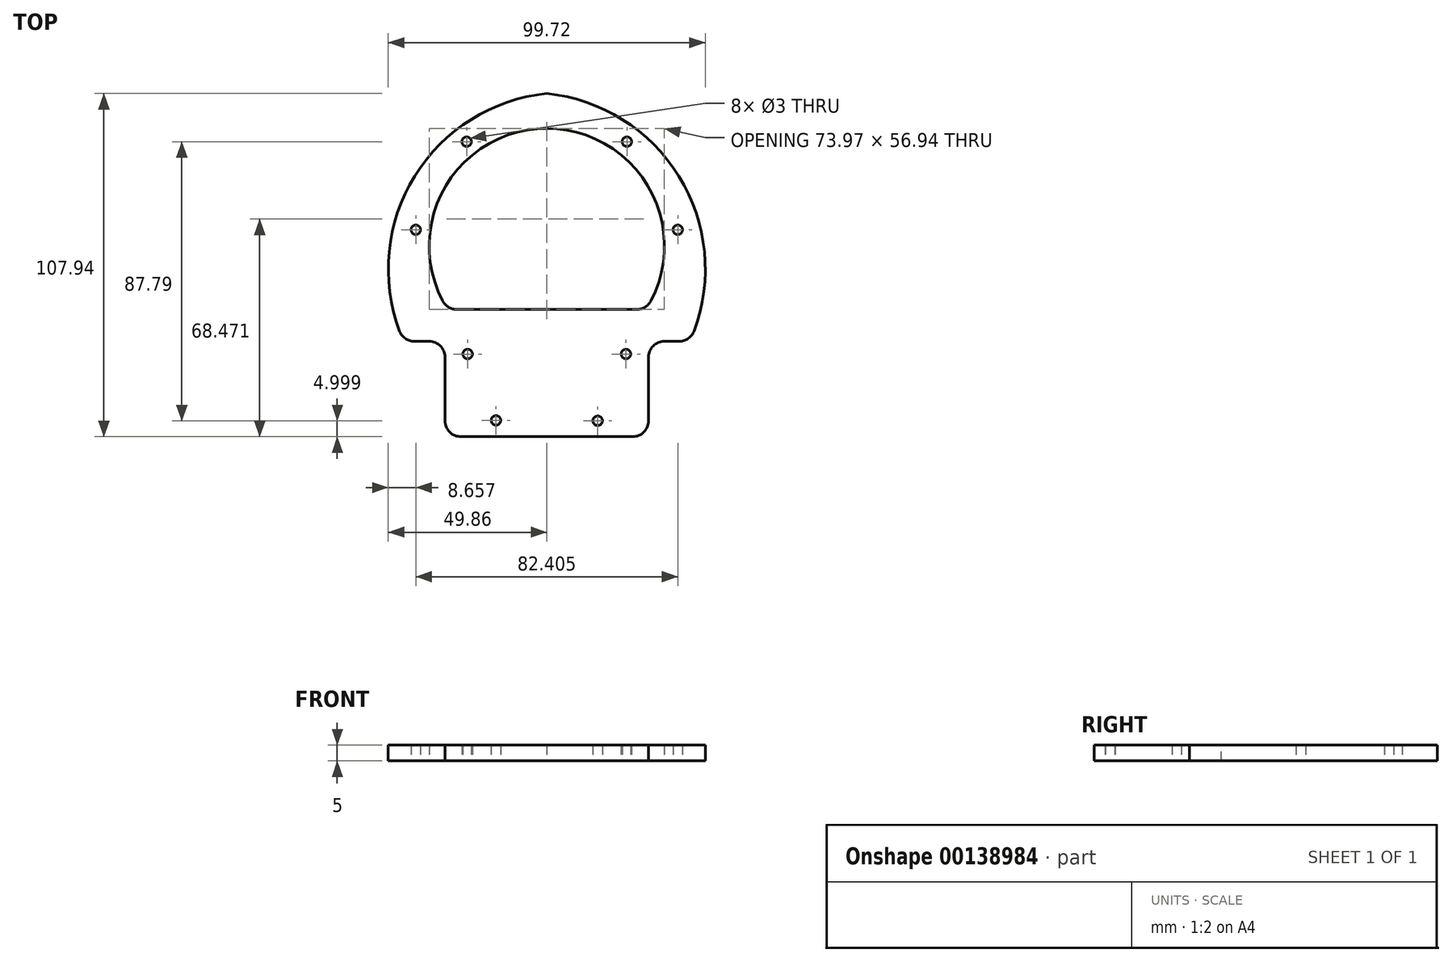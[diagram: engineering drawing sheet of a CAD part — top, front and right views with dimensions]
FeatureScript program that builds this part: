
annotation { "Feature Type Name" : "Feature", "Feature Type Description" : "" }
export const myFeature = defineFeature(function(context is Context, id is Id, definition is map)
    precondition{}
    {
        {
            var Q0;
            Q0=qCreatedBy(makeId("Top.planeOp"),FACE);
            var sketch = newSketch(context, id + "F0", { "sketchPlane" : qUnion([Q0])});
            skLineSegment(sketch, "E0.0", {"start": v(45, -25.98) * mm, "end": v(-45, -25.98) * mm});
            skLineSegment(sketch, "E0.1", {"start": v(-45, -25.98) * mm, "end": v(0, 51.96) * mm});
            skLineSegment(sketch, "E0.2", {"start": v(0, 51.96) * mm, "end": v(45, -25.98) * mm});
            skPoint(sketch, "E0.0.midPoint", {"position": v(0, -25.98) * mm});
            skLineSegment(sketch, "E1", {"start": v(-22.5, 13) * mm, "end": v(-42.42, 24.5) * mm, "construction": true});
            skArc(sketch, "E2", {"start": v(0, 51.96) * mm, "mid": v(-42.42, 24.5) * mm, "end": v(-45, -25.98) * mm});
            skLineSegment(sketch, "E3", {"start": v(22.5, 13) * mm, "end": v(42.42, 24.5) * mm, "construction": true});
            skArc(sketch, "E4", {"start": v(45, -25.98) * mm, "mid": v(42.42, 24.5) * mm, "end": v(0, 51.96) * mm});
            skLineSegment(sketch, "E5", {"start": v(0, -25.98) * mm, "end": v(0, -19.98) * mm, "construction": true});
            skCircle(sketch, "E6", {"center": v(0, 3.96) * mm, "radius": 37 * mm});
            skLineSegment(sketch, "E7", {"start": v(-22.5, 13) * mm, "end": v(0, 0) * mm, "construction": true});
            skLineSegment(sketch, "E8", {"start": v(0, 0) * mm, "end": v(22.5, 13) * mm, "construction": true});
            skPoint(sketch, "E9", {"position": v(0, -40.96) * mm});
            skLineSegment(sketch, "E10.bottom", {"start": v(-32, -15.98) * mm, "end": v(32, -15.98) * mm});
            skLineSegment(sketch, "E10.top", {"start": v(-32, -55.98) * mm, "end": v(32, -55.98) * mm});
            skLineSegment(sketch, "E10.left", {"start": v(-32, -15.98) * mm, "end": v(-32, -55.98) * mm});
            skLineSegment(sketch, "E10.right", {"start": v(32, -15.98) * mm, "end": v(32, -55.98) * mm});
            skPoint(sketch, "E11", {"position": v(0, -15.98) * mm});
            skCircle(sketch, "E12", {"center": v(-16, -50.86) * mm, "radius": 1.5 * mm});
            skCircle(sketch, "E13", {"center": v(16, -50.98) * mm, "radius": 1.5 * mm});
            skLineSegment(sketch, "E14", {"start": v(-16, -50.86) * mm, "end": v(16, -50.98) * mm, "construction": true});
            skPoint(sketch, "E15", {"position": v(0, -50.92) * mm});
            skCircle(sketch, "E16", {"center": v(-25.2, 36.8) * mm, "radius": 1.5 * mm});
            skCircle(sketch, "E17", {"center": v(-41.2, 9.1) * mm, "radius": 1.5 * mm});
            skLineSegment(sketch, "E18", {"start": v(-16.1, 52.58) * mm, "end": v(-54.25, -13.5) * mm, "construction": true});
            skLineSegment(sketch, "E19", {"start": v(0, -10.47) * mm, "end": v(0, 61.8) * mm, "construction": true});
            skCircle(sketch, "E20.MirrorC", {"center": v(25.2, 36.8) * mm, "radius": 1.5 * mm});
            skCircle(sketch, "E21.MirrorC", {"center": v(41.2, 9.1) * mm, "radius": 1.5 * mm});
            skLineSegment(sketch, "E22", {"start": v(25.2, 36.8) * mm, "end": v(41.2, 9.1) * mm, "construction": true});
            skCircle(sketch, "E23", {"center": v(-24.9, -29.98) * mm, "radius": 1.5 * mm});
            skCircle(sketch, "E24", {"center": v(24.9, -29.98) * mm, "radius": 1.5 * mm});
            skLineSegment(sketch, "E25", {"start": v(-24.9, -29.98) * mm, "end": v(24.9, -29.98) * mm, "construction": true});
            skPoint(sketch, "E26", {"position": v(0, -29.98) * mm});
            skSolve(sketch);
        }
        {
            var Q0;
            {var subQ0=sQuery(id+"F0.wireOp",EDGE,"E2");Q0=makeQuery(id+"F0.imprint","IMPRINT",FACE,{"disambiguationData":[TD([[makeQuery(id+"F0.imprint","IMPRINT",EDGE,{"derivedFrom":subQ0}),1.0]])]});}
            var Q1;
            {var subQ1=sQuery(id+"F0.wireOp",EDGE,"E0.1");var subQ3=sQuery(id+"F0.wireOp",EDGE,"E6");var subQ4=makeQuery(id+"F0.imprint","INTERSECT",VERTEX,{"disambiguationData":[OD(1.0)],"derivedFrom":[subQ1,subQ3]});Q1=makeQuery(id+"F0.imprint","IMPRINT",FACE,{"disambiguationData":[TD([[makeQuery(id+"F0.imprint","IMPRINT",EDGE,{"disambiguationData":[TD([[subQ4,1.0]])],"derivedFrom":subQ3}),-1.0]])]});}
            var Q2;
            {var subQ0=sQuery(id+"F0.wireOp",EDGE,"E4");Q2=makeQuery(id+"F0.imprint","IMPRINT",FACE,{"disambiguationData":[TD([[makeQuery(id+"F0.imprint","IMPRINT",EDGE,{"derivedFrom":subQ0}),1.0]])]});}
            var Q3;
            {var subQ13=sQuery(id+"F0.wireOp",EDGE,"8JRTccjr-kDRW-iMPo-pbyM-UjpLYdR7sCPQ.top");Q3=makeQuery(id+"F0.imprint","IMPRINT",FACE,{"disambiguationData":[TD([[makeQuery(id+"F0.imprint","IMPRINT",EDGE,{"derivedFrom":subQ13}),-1.0]])]});}
            var Q4;
            {var subQ5=sQuery(id+"F0.wireOp",EDGE,"8JRTccjr-kDRW-iMPo-pbyM-UjpLYdR7sCPQ.bottom");Q4=makeQuery(id+"F0.imprint","IMPRINT",FACE,{"disambiguationData":[TD([[makeQuery(id+"F0.imprint","IMPRINT",EDGE,{"derivedFrom":subQ5}),-1.0]])]});}
            var Q5;
            {var subQ0=sQuery(id+"F0.wireOp",EDGE,"8JRTccjr-kDRW-iMPo-pbyM-UjpLYdR7sCPQ.left");var subQ1=sQuery(id+"F0.wireOp",EDGE,"E0.0");var subQ2=makeQuery(id+"F0.imprint","INTERSECT",VERTEX,{"derivedFrom":[subQ1,subQ0]});Q5=makeQuery(id+"F0.imprint","IMPRINT",FACE,{"disambiguationData":[TD([[makeQuery(id+"F0.imprint","IMPRINT",EDGE,{"disambiguationData":[TD([[subQ2,-1.0]])],"derivedFrom":subQ1}),-1.0]])]});}
            var Q6;
            {var subQ5=sQuery(id+"F0.wireOp",EDGE,"8JRTccjr-kDRW-iMPo-pbyM-UjpLYdR7sCPQ.top");Q6=makeQuery(id+"F0.imprint","IMPRINT",FACE,{"disambiguationData":[TD([[makeQuery(id+"F0.imprint","IMPRINT",EDGE,{"derivedFrom":subQ5}),1.0]])]});}
            var Q7;
            {var subQ0=sQuery(id+"F0.wireOp",EDGE,"E6");var subQ1=sQuery(id+"F0.wireOp",EDGE,"vwtUNxXE-5amK-ixxl-kl4G-om5iWZnCJFOI");var subQ2=makeQuery(id+"F0.imprint","INTERSECT",VERTEX,{"disambiguationData":[OD(0.0)],"derivedFrom":[subQ1,subQ0]});Q7=makeQuery(id+"F0.imprint","IMPRINT",FACE,{"disambiguationData":[TD([[makeQuery(id+"F0.imprint","IMPRINT",EDGE,{"disambiguationData":[TD([[subQ2,-1.0]])],"derivedFrom":subQ1}),1.0]])]});}
            var Q8;
            {var subQ0=sQuery(id+"F0.wireOp",EDGE,"E6");var subQ1=sQuery(id+"F0.wireOp",EDGE,"E0.0");var subQ2=makeQuery(id+"F0.imprint","INTERSECT",VERTEX,{"disambiguationData":[OD(0.0)],"derivedFrom":[subQ1,subQ0]});Q8=makeQuery(id+"F0.imprint","IMPRINT",FACE,{"disambiguationData":[TD([[makeQuery(id+"F0.imprint","IMPRINT",EDGE,{"disambiguationData":[TD([[subQ2,-1.0]])],"derivedFrom":subQ1}),1.0]])]});}
            var Q9;
            {var subQ0=sQuery(id+"F0.wireOp",EDGE,"E6");var subQ1=sQuery(id+"F0.wireOp",EDGE,"E0.1");var subQ2=makeQuery(id+"F0.imprint","INTERSECT",VERTEX,{"disambiguationData":[OD(0.0)],"derivedFrom":[subQ1,subQ0]});Q9=makeQuery(id+"F0.imprint","IMPRINT",FACE,{"disambiguationData":[TD([[makeQuery(id+"F0.imprint","IMPRINT",EDGE,{"disambiguationData":[TD([[subQ2,-1.0]])],"derivedFrom":subQ0}),-1.0]])]});}
            var Q10;
            {var subQ0=sQuery(id+"F0.wireOp",EDGE,"E6");var subQ1=sQuery(id+"F0.wireOp",EDGE,"E0.2");var subQ2=makeQuery(id+"F0.imprint","INTERSECT",VERTEX,{"disambiguationData":[OD(1.0)],"derivedFrom":[subQ1,subQ0]});Q10=makeQuery(id+"F0.imprint","IMPRINT",FACE,{"disambiguationData":[TD([[makeQuery(id+"F0.imprint","IMPRINT",EDGE,{"disambiguationData":[TD([[subQ2,1.0]])],"derivedFrom":subQ0}),-1.0]])]});}
            var Q11;
            {var subQ0=sQuery(id+"F0.wireOp",EDGE,"E10.top");Q11=makeQuery(id+"F0.imprint","IMPRINT",FACE,{"disambiguationData":[TD([[makeQuery(id+"F0.imprint","IMPRINT",EDGE,{"derivedFrom":subQ0}),1.0]])]});}
            extrude(context, id + "F1", {"entities" : qUnion([Q0, Q1, Q2, Q3, Q4, Q5, Q6, Q7, Q8, Q9, Q10, Q11]), "depth" : 5 * mm});
        }
        {
            var Q0;
            Q0=makeQuery(id+"F1.opExtrude","SWEPT_EDGE",EDGE,{"disambiguationData":[OSD([sQuery(id+"F0.wireOp",EDGE,"E0.0"),sQuery(id+"F0.wireOp",EDGE,"E10.left")])]});
            var Q1;
            Q1=makeQuery(id+"F1.opExtrude","SWEPT_EDGE",EDGE,{"disambiguationData":[OSD([sQuery(id+"F0.wireOp",EDGE,"E0.0"),sQuery(id+"F0.wireOp",EDGE,"E0.1"),sQuery(id+"F0.wireOp",EDGE,"E2")])]});
            var Q2;
            Q2=makeQuery(id+"F1.opExtrude","SWEPT_EDGE",EDGE,{"disambiguationData":[OSD([sQuery(id+"F0.wireOp",EDGE,"E0.0"),sQuery(id+"F0.wireOp",EDGE,"E10.right")])]});
            var Q3;
            Q3=makeQuery(id+"F1.opExtrude","SWEPT_EDGE",EDGE,{"disambiguationData":[OSD([sQuery(id+"F0.wireOp",EDGE,"E0.0"),sQuery(id+"F0.wireOp",EDGE,"E0.2"),sQuery(id+"F0.wireOp",EDGE,"E4")])]});
            var Q4;
            Q4=makeQuery(id+"F1.opExtrude","SWEPT_EDGE",EDGE,{"disambiguationData":[OSD([sQuery(id+"F0.wireOp",EDGE,"E10.top"),sQuery(id+"F0.wireOp",EDGE,"E10.left")])]});
            var Q5;
            Q5=makeQuery(id+"F1.opExtrude","SWEPT_EDGE",EDGE,{"disambiguationData":[OSD([sQuery(id+"F0.wireOp",EDGE,"E10.top"),sQuery(id+"F0.wireOp",EDGE,"E10.right")])]});
            var Q6;
            {var subQ0=sQuery(id+"F0.wireOp",EDGE,"E10.bottom");var subQ1=sQuery(id+"F0.wireOp",EDGE,"E6");Q6=makeQuery(id+"F1.opExtrude","SWEPT_EDGE",EDGE,{"disambiguationData":[OSD([subQ1,subQ0]),TDD([makeQuery(id+"F0.imprint","INTERSECT",VERTEX,{"disambiguationData":[OD(0.0)],"derivedFrom":[subQ1,subQ0]})])]});}
            var Q7;
            {var subQ0=sQuery(id+"F0.wireOp",EDGE,"E10.bottom");var subQ1=sQuery(id+"F0.wireOp",EDGE,"E6");Q7=makeQuery(id+"F1.opExtrude","SWEPT_EDGE",EDGE,{"disambiguationData":[OSD([subQ1,subQ0]),TDD([makeQuery(id+"F0.imprint","INTERSECT",VERTEX,{"disambiguationData":[OD(1.0)],"derivedFrom":[subQ1,subQ0]})])]});}
            fillet(context, id + "F2", {"entities" : qUnion([Q0, Q1, Q2, Q3, Q4, Q5, Q6, Q7]), "radius" : 5 * mm, "tangentPropagation" : true, "allowEdgeOverflow" : false});
        }
    });
